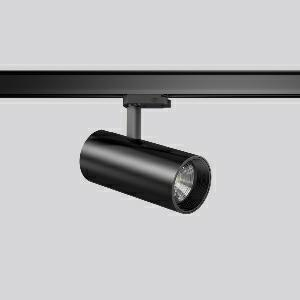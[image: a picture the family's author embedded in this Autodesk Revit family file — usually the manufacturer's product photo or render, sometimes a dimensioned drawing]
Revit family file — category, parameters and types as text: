
# Revit family: deecos_s_mini_742209_003_1_d1b4
name_source: partatom
category: Lighting Fixtures
units: mm (PartAtom-declared; Revit-internal decimal feet)

## family parameters
Cut with Voids When Loaded = No
Host = Face
Light Source = No
Part Type = Normal
Room Calculation Point = No
Round Connector Dimension = Use Diameter
Shared = No

## types (1)
- DEECOS S mini (1 x LED Modul 940, 3500 lm, 4000)
    Apparent Load = 29 VA
    Approval mark = CE
    CIE Flux Codes = 80 99 100 100 100
    Color Rendering = 92
    Color Temperature = 4000
    Default Elevation = 1800 mm
    Description = Series: DEECOS S mini
LED surface-mounted projector in modern design with no visible cooling ribs. Housing: die-cast aluminium, powder-coated. Rotation range: 356°. Swivel range: 90°. Black plastic ring and recessed LED to prevent glare from the side. Optical assembly with lens made of plastic (polycarbonate) for the best homogeneous light distribution - can be changed without tools. Best colour rendering index Ra>90. With multi adaptor for 3-circuit tracks 230 V. Suitable for Track on ceiling, Wall track. High quality converter without flickering and stroboscopic effect. The following accessories can be mounted without use of tools: interchangeable lenses, decorative glasses, honeycomb louvre, clear and frosted diffusers, white interchangeable plastic ring. 
Colour: deep black, matt (RAL 9005)
Diameter: 87 mm
Height: 214 mm
Lamp: LED
Socket: without socket
Colour temperature: 4000K
Colour rendering index (CRI): 92
System power: 29 W
Rated luminous flux: 3500 lm
Luminous efficiency: 121 lm/W
Control gear: Regulated power supply
Protection class: I
Type of protection: IP 20
    Height = 214 mm
    Lamp = 1 x LED Modul 940
    Lamp Light Flux = 3500 lm
    Lamp count = 1
    Length = 87 mm
    Lifetime = 50000 h
    Luminous efficacy = 121 lm/W
    Manufacturer = RZB
    ModVariant = No
    Model = 742209.003.1
    Mounting Place = Ceiling
    Mounting Type = Rail mounted
    Number of Poles = 1
    OnlyDefault = Yes
    Power Factor = 1
    Product Name = DEECOS S mini
    Product group = Track mounted projectors
    ProductGroupID = 301
    Protection Class = Protection class I
    Protection Degree = IP 20
    RLX_Detail_Level = 1
    RLX_Emergency_Light_Flux = 0 lm
    RLX_Emergency_Type = 0
    RLX_Emergency_Type_DB = No
    RlxData = <blob elided: 38901 chars, md5=e550f696>
    Socket = socket
    Standby Power = 0 W
    System Light Flux = 3500 lm
    System Power = 29 W
    Type Comments = Product without accessories
    Type Image = 741930.003.jpg
    URL = http://relux.com
    VarID = ---
    Voltage = 230 V
    Voltage Range = 220-240 V
    Weight = 0.00 kg
    Width = 0 mm  [stored 0 ft]

note: [stored X ft] marks values corroborated as IEEE doubles in the binary element streams (Revit-internal decimal feet)

## geometry (parser evidence)
native form markers: Blend x4, Sweep x11
no freeform markers — native parametric forms only
